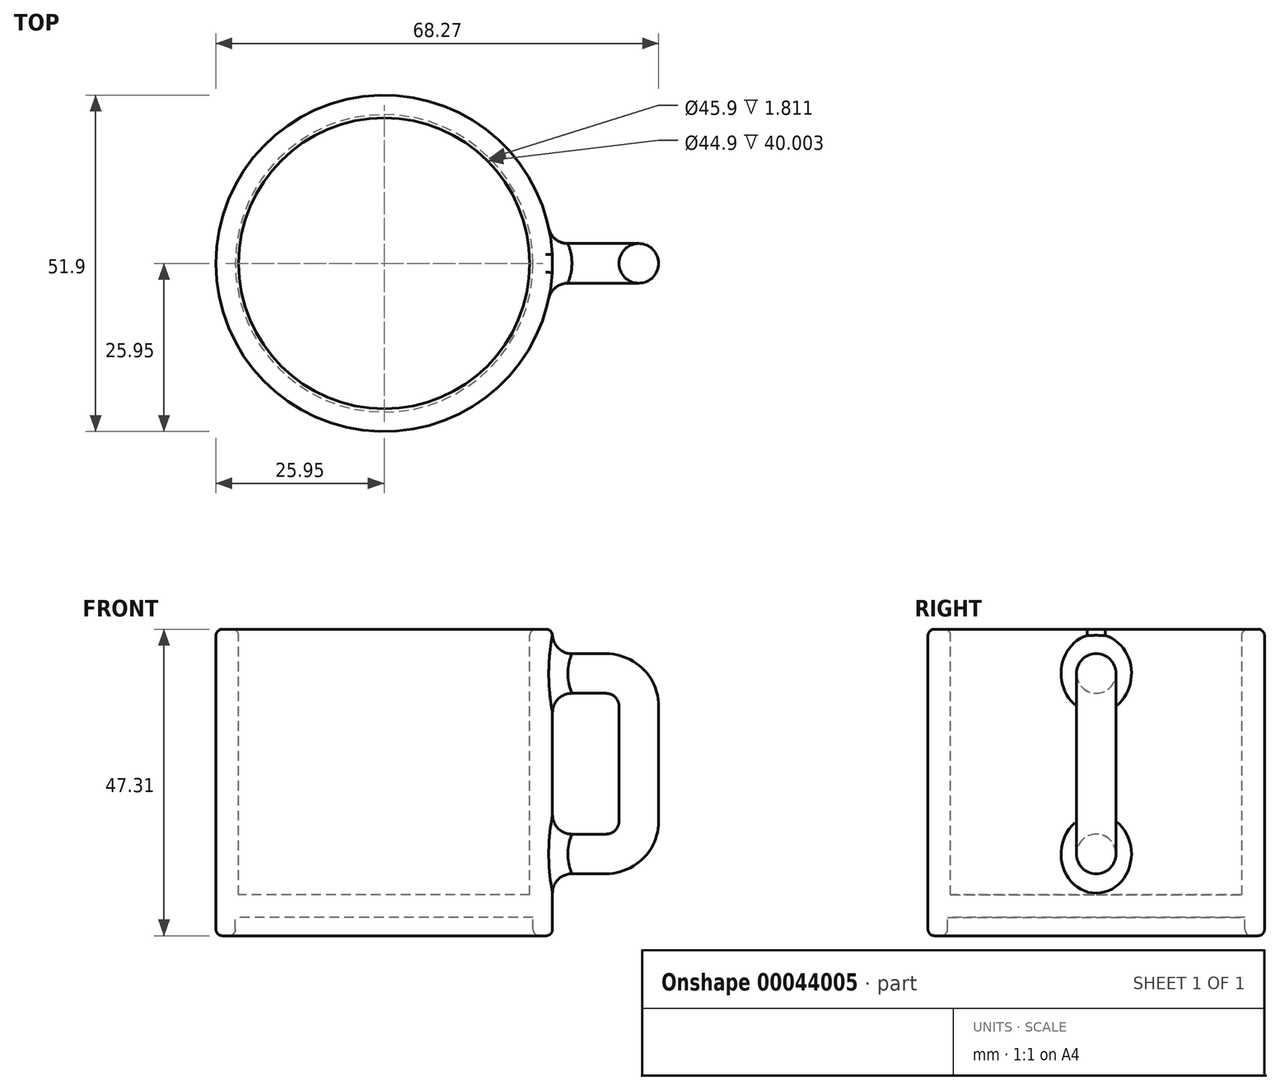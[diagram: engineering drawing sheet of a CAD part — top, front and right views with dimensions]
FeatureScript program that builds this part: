
annotation { "Feature Type Name" : "Feature", "Feature Type Description" : "" }
export const myFeature = defineFeature(function(context is Context, id is Id, definition is map)
    precondition{}
    {
        {
            var Q0;
            Q0=qCreatedBy(makeId("Front.planeOp"),FACE);
            var sketch = newSketch(context, id + "F0", { "sketchPlane" : qUnion([Q0])});
            skLineSegment(sketch, "E0.bottom", {"start": v(0, 47.31) * mm, "end": v(25.95, 47.31) * mm});
            skLineSegment(sketch, "E0.top", {"start": v(0, 0) * mm, "end": v(25.95, 0) * mm});
            skLineSegment(sketch, "E0.left", {"start": v(0, 47.31) * mm, "end": v(0, 0) * mm});
            skLineSegment(sketch, "E0.right", {"start": v(25.95, 47.31) * mm, "end": v(25.95, 0) * mm});
            skLineSegment(sketch, "E1.bottom", {"start": v(0, 0) * mm, "end": v(22.95, 0) * mm});
            skLineSegment(sketch, "E1.top", {"start": v(0, 2.81) * mm, "end": v(22.95, 2.81) * mm});
            skLineSegment(sketch, "E1.left", {"start": v(0, 0) * mm, "end": v(0, 2.81) * mm});
            skLineSegment(sketch, "E1.right", {"start": v(22.95, 0) * mm, "end": v(22.95, 2.81) * mm});
            skSolve(sketch);
        }
        {
            var Q0;
            Q0=qCreatedBy(makeId("Front.planeOp"),FACE);
            var sketch = newSketch(context, id + "F1", { "sketchPlane" : qUnion([Q0])});
            skLineSegment(sketch, "E2.bottom", {"start": v(0, 40.43) * mm, "end": v(34.22, 40.43) * mm});
            skLineSegment(sketch, "E2.top", {"start": v(0, 12.67) * mm, "end": v(34.22, 12.67) * mm});
            skLineSegment(sketch, "E2.left", {"start": v(0, 40.43) * mm, "end": v(0, 12.67) * mm});
            skLineSegment(sketch, "E2.right", {"start": v(39.22, 35.43) * mm, "end": v(39.22, 17.67) * mm});
            skPoint(sketch, "E3.visualSharp", {"position": v(39.22, 40.43) * mm});
            skArc(sketch, "E3.filletArc", {"start": v(39.22, 35.43) * mm, "mid": v(37.76, 38.96) * mm, "end": v(34.22, 40.43) * mm});
            skPoint(sketch, "E4.visualSharp", {"position": v(39.22, 12.67) * mm});
            skArc(sketch, "E4.filletArc", {"start": v(34.22, 12.67) * mm, "mid": v(37.76, 14.14) * mm, "end": v(39.22, 17.67) * mm});
            skSolve(sketch);
        }
        {
            var Q0;
            Q0=makeQuery(id+"F0.imprint","IMPRINT",FACE,{"disambiguationData":[TD([[makeQuery(id+"F0.imprint","IMPRINT",EDGE,{"derivedFrom":sQuery(id+"F0.wireOp",EDGE,"E0.bottom")}),-1.0]])]});
            var Q1;
            Q1=sQuery(id+"F0.wireOp",EDGE,"E0.left");
            revolve(context, id + "F2", {"entities" : qUnion([Q0]), "axis" : qUnion([Q1]), "revolveType" : RevolveType.FULL});
        }
        {
            var Q0;
            Q0=qCreatedBy(makeId("Right.planeOp"),FACE);
            var sketch = newSketch(context, id + "F3", { "sketchPlane" : qUnion([Q0])});
            skCircle(sketch, "E5", {"center": v(0, 12.63) * mm, "radius": 3.06 * mm});
            skSolve(sketch);
        }
        {
            var Q0;
            Q0=makeQuery(id+"F3.imprint","IMPRINT",FACE,{"disambiguationData":[TD([[makeQuery(id+"F3.imprint","IMPRINT",EDGE,{"derivedFrom":sQuery(id+"F3.wireOp",EDGE,"E5")}),1.0]])]});
            var Q1;
            Q1=sQuery(id+"F1.wireOp",EDGE,"E2.top");
            var Q2;
            Q2=sQuery(id+"F1.wireOp",EDGE,"E4.filletArc");
            var Q3;
            Q3=sQuery(id+"F1.wireOp",EDGE,"E2.right");
            var Q4;
            Q4=sQuery(id+"F1.wireOp",EDGE,"E3.filletArc");
            var Q5;
            Q5=sQuery(id+"F1.wireOp",EDGE,"E2.bottom");
            sweep(context, id + "F4", {"profiles" : qUnion([Q0]), "path" : qUnion([Q1, Q2, Q3, Q4, Q5])});
        }
        {
            var Q0;
            Q0=makeQuery(id+"F4.opSweep","SWEPT_BODY",BODY,{"disambiguationData":[OSD([sQuery(id+"F1.wireOp",EDGE,"E2.bottom"),sQuery(id+"F3.wireOp",EDGE,"E5")])]});
            var Q1;
            Q1=makeQuery(id+"F2.opRevolve","SWEPT_BODY",BODY,{"disambiguationData":[OSD([sQuery(id+"F0.wireOp",EDGE,"E0.bottom"),sQuery(id+"F0.wireOp",EDGE,"E0.top"),sQuery(id+"F0.wireOp",EDGE,"E0.left"),sQuery(id+"F0.wireOp",EDGE,"E0.right"),sQuery(id+"F0.wireOp",EDGE,"E1.top"),sQuery(id+"F0.wireOp",EDGE,"E1.right")])]});
            booleanBodies(context, id + "F5", {"operationType" : BooleanOperationType.UNION, "tools" : qUnion([Q0, Q1])});
        }
        {
            var Q0;
            Q0=makeQuery(id+"F2.opRevolve","SWEPT_FACE",FACE,{"disambiguationData":[OSD([sQuery(id+"F0.wireOp",EDGE,"E0.bottom")])]});
            shell(context, id + "F6", {"entities" : qUnion([Q0]), "thickness" : 3.5 * mm});
        }
        {
            var Q0;
            Q0=makeQuery(id+"F5.opBoolean","INTERSECT",EDGE,{"derivedFrom":[makeQuery(id+"F2.opRevolve","SWEPT_FACE",FACE,{"disambiguationData":[OSD([sQuery(id+"F0.wireOp",EDGE,"E0.right")])]}),makeQuery(id+"F4.opSweep","SWEPT_FACE",FACE,{"disambiguationData":[OSD([sQuery(id+"F1.wireOp",EDGE,"E2.top"),sQuery(id+"F3.wireOp",EDGE,"E5")])]})]});
            var Q1;
            Q1=makeQuery(id+"F5.opBoolean","INTERSECT",EDGE,{"derivedFrom":[makeQuery(id+"F2.opRevolve","SWEPT_FACE",FACE,{"disambiguationData":[OSD([sQuery(id+"F0.wireOp",EDGE,"E0.right")])]}),makeQuery(id+"F4.opSweep","SWEPT_FACE",FACE,{"disambiguationData":[OSD([sQuery(id+"F1.wireOp",EDGE,"E2.bottom"),sQuery(id+"F3.wireOp",EDGE,"E5")])]})]});
            fillet(context, id + "F7", {"entities" : qUnion([Q0, Q1]), "radius" : 3 * mm, "tangentPropagation" : true, "allowEdgeOverflow" : false});
        }
        {
            var Q0;
            Q0=makeQuery(id+"F6.opShell","OFFSET_EDGE",EDGE,{"disambiguationData":[OSD([sQuery(id+"F0.wireOp",EDGE,"E0.bottom"),sQuery(id+"F0.wireOp",EDGE,"E0.right")])]});
            var Q1;
            Q1=makeQuery(id+"F2.opRevolve","SWEPT_EDGE",EDGE,{"disambiguationData":[OSD([sQuery(id+"F0.wireOp",EDGE,"E0.bottom"),sQuery(id+"F0.wireOp",EDGE,"E0.right")])]});
            var Q2;
            Q2=makeQuery(id+"F2.opRevolve","SWEPT_EDGE",EDGE,{"disambiguationData":[OSD([sQuery(id+"F0.wireOp",EDGE,"E0.top"),sQuery(id+"F0.wireOp",EDGE,"E0.right")])]});
            var Q3;
            Q3=makeQuery(id+"F2.opRevolve","SWEPT_EDGE",EDGE,{"disambiguationData":[OSD([sQuery(id+"F0.wireOp",EDGE,"E0.top"),sQuery(id+"F0.wireOp",EDGE,"E1.bottom"),sQuery(id+"F0.wireOp",EDGE,"E1.right")])]});
            fillet(context, id + "F8", {"entities" : qUnion([Q0, Q1, Q2, Q3]), "radius" : 1 * mm, "tangentPropagation" : true, "allowEdgeOverflow" : false});
        }
    });
